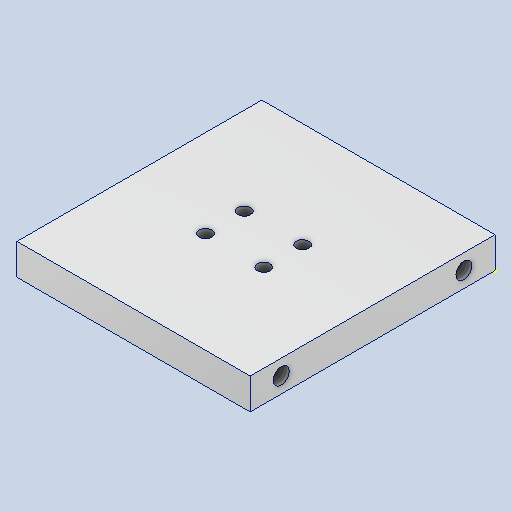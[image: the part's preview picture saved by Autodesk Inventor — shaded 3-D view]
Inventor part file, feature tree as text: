
AUTODESK INVENTOR PART (.ipt)
format: ipt  version: 2023 (Build 270158000, 158)  size: 268,800 bytes
history: native  units: mm
features: sketch x5, hole x3, extrude x1
ambient origin geometry x8: Origin, YZ Plane, XZ Plane, XY Plane, X Axis, Y Axis, Z Axis, Center Point
bodies: Solid1 (feature_tree)
feature tree (9):
  extrude  "Extrusion1"  Depth=63.0mm
  hole  "Furo1"  [1 undecoded]
  sketch  "Sketch3"  dims[d6=15.0mm d7=0.0mm]
  hole  "Hole2"  [1 undecoded]
  hole  "Hole3"  [1 undecoded]
  sketch  "Sketch1"  dims[d0=60.0mm d1=63.0mm]
  sketch  "Esboço2"  dims[d2=8.0mm d3=0.0mm d5=0.0mm]
  sketch  "Sketch4"  dims[d8=15.0mm d9=10.0mm]
  sketch  "Sketch5"  dims[d10=0.0mm d11=60.0mm d12=22.5mm d13=3.242mm d14=8.0mm d15=4.0mm d16=2.0mm d17=90.0deg d18=0.5mm d19=20.594885mm d20=26.0mm d21=8.0mm d22=8.0mm d23=4.134mm d24=10.0mm d25=4.0mm d26=2.0mm d27=90.0deg d28=14.2mm d29=20.594885mm d30=4.134mm d31=10.0mm d32=4.0mm d33=2.0mm d34=90.0deg d35=14.2mm d36=20.594885mm]
note: 3 required parameter values undecoded (feature->parameter linkage not recoverable at this tier; creation-order binding heuristic only, values carry confidence <= 0.55)
